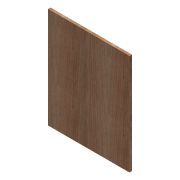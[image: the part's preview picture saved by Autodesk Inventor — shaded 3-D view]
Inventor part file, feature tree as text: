
AUTODESK INVENTOR PART (.ipt)
format: ipt  version: 2013 (Build 170138000, 138)  size: 87,552 bytes
history: native  units: in
note: dims shown in document units (in); Inventor stores cm internally (conversion verified against a paired STEP export)
features: extrude x1, sketch x1
ambient origin geometry x8: Origin, YZ Plane, XZ Plane, XY Plane, X Axis, Y Axis, Z Axis, Center Point
bodies: Solid1 (feature_tree)
feature tree (2):
  extrude  "Extrusion1"  Depth=21.5in
  sketch  "Sketch1"  dims[d0=16.15in d2=21.5in d3=0.5in d4=0.0in]
